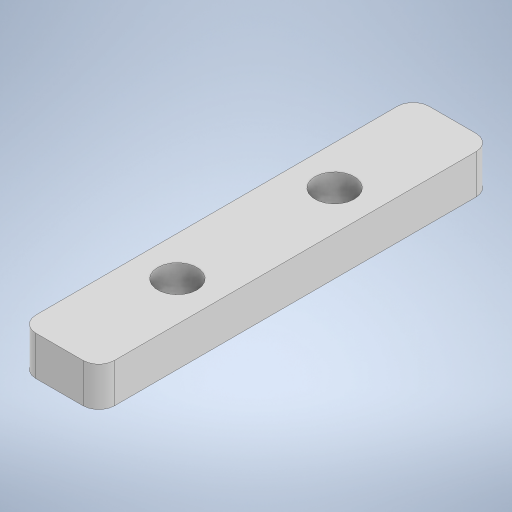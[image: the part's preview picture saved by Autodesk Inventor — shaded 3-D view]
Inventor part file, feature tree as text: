
AUTODESK INVENTOR PART (.ipt)
format: ipt  version: 2023 (Build 270158000, 158)  size: 221,696 bytes
history: native  units: in
note: dims shown in document units (in); Inventor stores cm internally (conversion verified against a paired STEP export)
features: extrude x1, fillet x1, sketch x1
ambient origin geometry x8: Origin, YZ Plane, XZ Plane, XY Plane, X Axis, Y Axis, Z Axis, Center Point
bodies: Solid1 (feature_tree)
feature tree (3):
  extrude  "Extrusion1"  Depth=0.1969in
  fillet  "Fillet1"  Radius=0.3937in
  sketch  "Sketch1"  dims[d0=0.3937in d1=0.1969in d2=0.3937in d3=1.9685in d4=0.1969in d5=0.0in d6=0.0787in]
